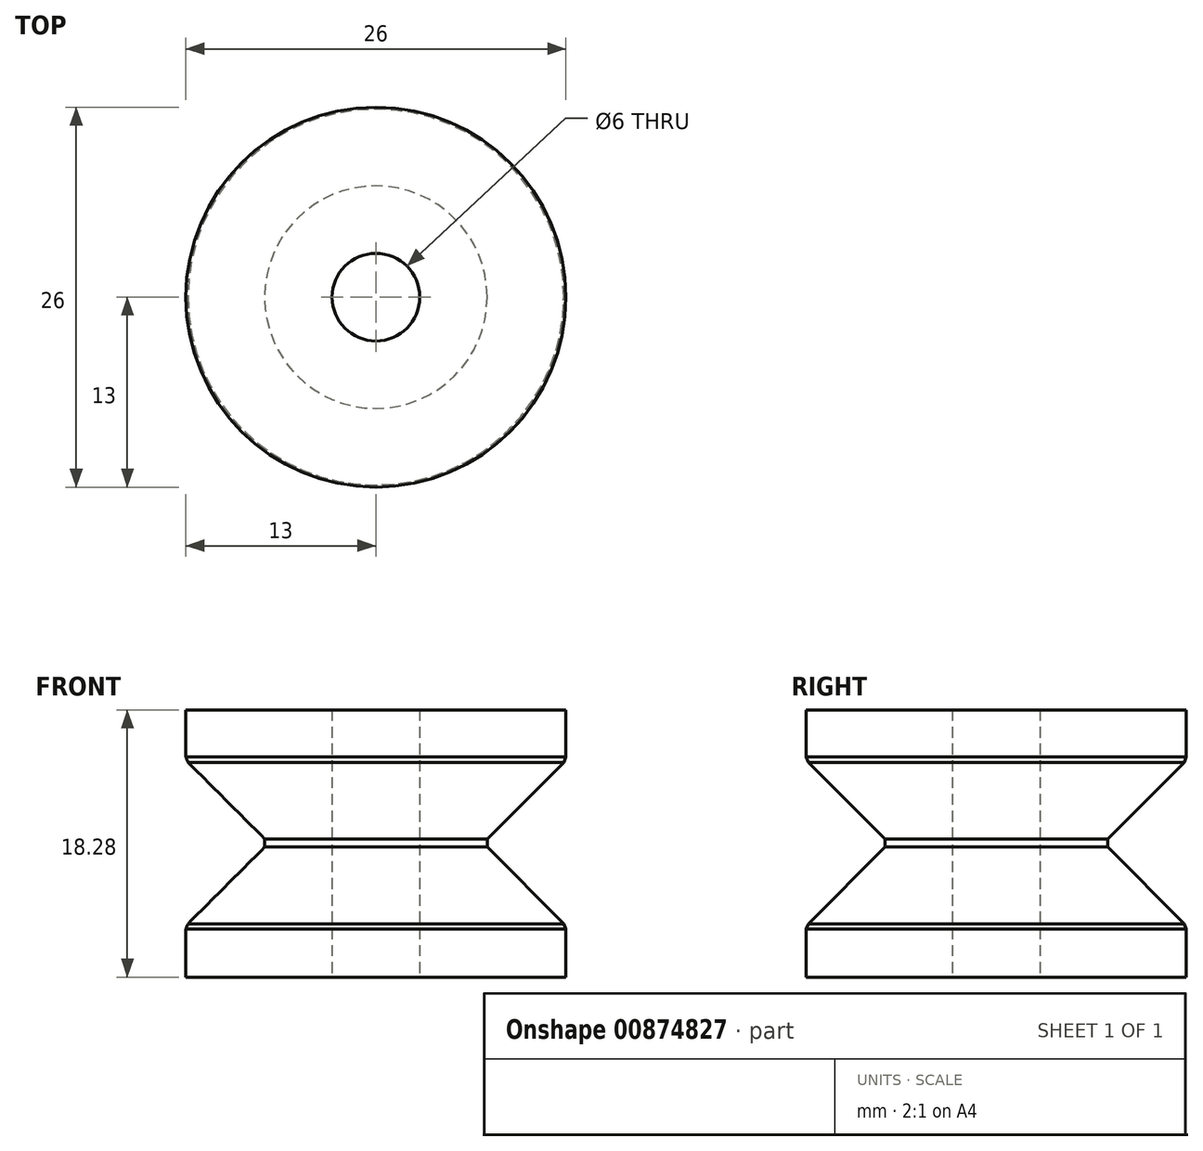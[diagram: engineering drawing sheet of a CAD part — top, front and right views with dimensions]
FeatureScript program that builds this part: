
annotation { "Feature Type Name" : "Feature", "Feature Type Description" : "" }
export const myFeature = defineFeature(function(context is Context, id is Id, definition is map)
    precondition{}
    {
        {
            var Q0;
            Q0=qCreatedBy(makeId("Front.planeOp"),FACE);
            var sketch = newSketch(context, id + "F0", { "sketchPlane" : qUnion([Q0])});
            skPoint(sketch, "E0.endSnap0", {"position": v(-14.28, 7.14) * mm});
            skLineSegment(sketch, "E1", {"start": v(0, 0) * mm, "end": v(-7.14, 7.14) * mm});
            skPoint(sketch, "E2.endSnap0", {"position": v(0, 7.14) * mm});
            skPoint(sketch, "E3.orphan", {"position": v(-14.28, 14.28) * mm});
            skPoint(sketch, "E4.right.start.orphan", {"position": v(-14.28, 0) * mm});
            skPoint(sketch, "E4.bottom.end.orphan", {"position": v(-7.14, 0) * mm});
            skLineSegment(sketch, "E5", {"start": v(0, 0) * mm, "end": v(0, -2) * mm});
            skLineSegment(sketch, "E6", {"start": v(-7.14, 7.14) * mm, "end": v(-12.14, 7.14) * mm});
            skLineSegment(sketch, "E7", {"start": v(0, -2) * mm, "end": v(-12.14, -2) * mm});
            skLineSegment(sketch, "E8", {"start": v(-12.14, -2) * mm, "end": v(-12.14, 7.14) * mm});
            skPoint(sketch, "E9.end.orphan", {"position": v(15, 7.14) * mm});
            skPoint(sketch, "E9.start.orphan", {"position": v(7.14, 7.14) * mm});
            skPoint(sketch, "E10.end.orphan", {"position": v(0, 14.28) * mm});
            skPoint(sketch, "E10.start.orphan", {"position": v(-9.64, 14.28) * mm});
            skLineSegment(sketch, "E11", {"start": v(15, -2) * mm, "end": v(15, 7.14) * mm});
            skLineSegment(sketch, "E12", {"start": v(-12.14, 7.14) * mm, "end": v(-11.14, 7.14) * mm});
            skLineSegment(sketch, "E13", {"start": v(-11.14, 7.14) * mm, "end": v(-9.14, 7.14) * mm});
            skLineSegment(sketch, "E14", {"start": v(-9.14, 7.14) * mm, "end": v(-7.14, 7.14) * mm});
            skLineSegment(sketch, "E15", {"start": v(-11.14, 7.14) * mm, "end": v(-11.14, 6.14) * mm});
            skLineSegment(sketch, "E16", {"start": v(-11.14, 6.14) * mm, "end": v(-9.14, 6.14) * mm});
            skLineSegment(sketch, "E17", {"start": v(-9.14, 6.14) * mm, "end": v(-9.14, 7.14) * mm});
            skLineSegment(sketch, "E18", {"start": v(-3.57, 3.57) * mm, "end": v(-3.5, 3.64) * mm});
            skLineSegment(sketch, "E19", {"start": v(-3.5, 3.64) * mm, "end": v(-7.04, 7.18) * mm});
            skLineSegment(sketch, "E20", {"start": v(-3.5, 3.64) * mm, "end": v(0.04, 0.1) * mm});
            skLineSegment(sketch, "E21", {"start": v(-7.04, 7.18) * mm, "end": v(-4.2, 10) * mm});
            skLineSegment(sketch, "E22", {"start": v(-4.2, 10) * mm, "end": v(-3.5, 10.71) * mm});
            skLineSegment(sketch, "E23", {"start": v(0.04, 0.1) * mm, "end": v(2.86, 2.93) * mm});
            skLineSegment(sketch, "E24", {"start": v(-4.2, 10) * mm, "end": v(2.86, 2.93) * mm});
            skLineSegment(sketch, "E25", {"start": v(-3.5, 10.71) * mm, "end": v(-1.3, 8.52) * mm});
            skLineSegment(sketch, "E26.MirrorCS", {"start": v(-12.14, 16.28) * mm, "end": v(-12.14, 7.14) * mm});
            skLineSegment(sketch, "E27.MirrorCS", {"start": v(0, 16.28) * mm, "end": v(-12.14, 16.28) * mm});
            skLineSegment(sketch, "E28.MirrorCS", {"start": v(0, 14.28) * mm, "end": v(-7.14, 7.14) * mm});
            skLineSegment(sketch, "E29.MirrorCS", {"start": v(0, 14.28) * mm, "end": v(0, 16.28) * mm});
            skLineSegment(sketch, "E30.MirrorCS", {"start": v(-2.8, 11.42) * mm, "end": v(4.28, 4.35) * mm});
            skLineSegment(sketch, "E31.MirrorCS", {"start": v(3.57, 10.71) * mm, "end": v(0.04, 14.25) * mm});
            skLineSegment(sketch, "E32.MirrorCS", {"start": v(0.04, 14.25) * mm, "end": v(-2.8, 11.42) * mm});
            skLineSegment(sketch, "E33.MirrorCS", {"start": v(7.1, 7.18) * mm, "end": v(4.28, 4.35) * mm});
            skLineSegment(sketch, "E34.MirrorCS", {"start": v(3.57, 10.71) * mm, "end": v(7.1, 7.18) * mm});
            skLineSegment(sketch, "E35", {"start": v(0, 14.28) * mm, "end": v(2, 14.28) * mm});
            skLineSegment(sketch, "E36", {"start": v(3.57, 10.71) * mm, "end": v(3.85, 11) * mm});
            skLineSegment(sketch, "E37", {"start": v(3.85, 11) * mm, "end": v(2, 12.85) * mm});
            skLineSegment(sketch, "E38", {"start": v(2, 12.85) * mm, "end": v(2, 14.28) * mm});
            skLineSegment(sketch, "E39", {"start": v(2, 14.28) * mm, "end": v(2, 16.28) * mm});
            skLineSegment(sketch, "E40", {"start": v(0, 0) * mm, "end": v(2, 0) * mm});
            skLineSegment(sketch, "E41", {"start": v(2.86, 2.93) * mm, "end": v(3.15, 2.65) * mm});
            skLineSegment(sketch, "E42", {"start": v(3.15, 2.65) * mm, "end": v(2, 1.5) * mm});
            skLineSegment(sketch, "E43", {"start": v(2, 0) * mm, "end": v(2, 1.5) * mm});
            skLineSegment(sketch, "E44", {"start": v(7.1, 7.18) * mm, "end": v(7.39, 7.46) * mm});
            skLineSegment(sketch, "E45", {"start": v(7.1, 7.18) * mm, "end": v(7.39, 6.9) * mm});
            skLineSegment(sketch, "E46", {"start": v(3.15, 2.65) * mm, "end": v(7.39, 6.9) * mm});
            skLineSegment(sketch, "E47", {"start": v(7.39, 6.9) * mm, "end": v(7.39, 7.46) * mm});
            skLineSegment(sketch, "E48", {"start": v(7.39, 7.46) * mm, "end": v(3.85, 11) * mm});
            skLineSegment(sketch, "E49", {"start": v(2, 0) * mm, "end": v(2, -2) * mm});
            skLineSegment(sketch, "E50", {"start": v(2, -2) * mm, "end": v(12, -2) * mm});
            skLineSegment(sketch, "E51", {"start": v(2, 16.28) * mm, "end": v(12, 16.28) * mm});
            skLineSegment(sketch, "E52", {"start": v(12, 16.28) * mm, "end": v(12, -2) * mm});
            skSolve(sketch);
        }
        {
            var Q0;
            Q0=makeQuery(id+"F0.imprint","IMPRINT",FACE,{"disambiguationData":[TD([[makeQuery(id+"F0.imprint","IMPRINT",EDGE,{"derivedFrom":sQuery(id+"F0.wireOp",EDGE,"E37")}),-1.0]])]});
            var Q1;
            Q1=sQuery(id+"F0.wireOp",EDGE,"E11");
            revolve(context, id + "F1", {"surfaceOperationType" : NewSurfaceOperationType.NEW, "entities" : qUnion([Q0]), "axis" : qUnion([Q1]), "revolveType" : RevolveType.FULL});
        }
        {
            var Q0;
            Q0=makeQuery(id+"F1.opRevolve","SWEPT_EDGE",EDGE,{"disambiguationData":[OSD([sQuery(id+"F0.wireOp",EDGE,"E37"),sQuery(id+"F0.wireOp",EDGE,"E38")])]});
            var Q1;
            Q1=makeQuery(id+"F1.opRevolve","SWEPT_EDGE",EDGE,{"disambiguationData":[OSD([sQuery(id+"F0.wireOp",EDGE,"E42"),sQuery(id+"F0.wireOp",EDGE,"E43")])]});
            chamfer(context, id + "F2", {"entities" : qUnion([Q0, Q1]), "width" : 0.5 * mm, "tangentPropagation" : true});
        }
    });
